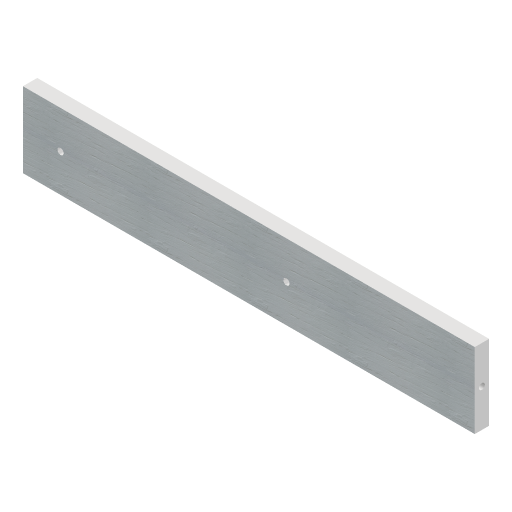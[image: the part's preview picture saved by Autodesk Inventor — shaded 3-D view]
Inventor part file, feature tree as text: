
AUTODESK INVENTOR PART (.ipt)
format: ipt  version: 2024 (Build 280153000, 153)  size: 188,928 bytes
history: native  units: in
note: dims shown in document units (in); Inventor stores cm internally (conversion verified against a paired STEP export)
features: extrude x5, sketch x5
ambient origin geometry x8: Origin, YZ Plane, XZ Plane, XY Plane, X Axis, Y Axis, Z Axis, Center Point
bodies: Solid1 (feature_tree)
feature tree (10):
  extrude  "Extrusion1"  Depth=3.937in
  extrude  "Extrusion2"  Depth=9.8425in
  extrude  "Extrusion3"  Depth=0.315in
  extrude  "Extrusion4"  Depth=0.4331in TaperAngle=0.0deg
  extrude  "Extrusion5"  Depth=0.4331in TaperAngle=0.0deg
  sketch  "Sketch1"  dims[d0=23.622in d1=3.937in]
  sketch  "Sketch2"  dims[d2=0.374in d3=0.374in d4=0.0in d5=0.0in d6=9.8425in]
  sketch  "Sketch3"  dims[d7=1.9685in d8=0.315in]
  sketch  "Sketch4"  dims[d9=0.315in d10=0.4331in d11=0.0in]
  sketch  "Sketch5"  dims[d12=0.315in d13=0.4331in d14=0.0in d15=0.315in d16=0.4331in d17=0.0in d18=1.9685in d19=6.5617in d20=6.5617in d21=6.5617in d22=1.9685in d23=0.315in d24=0.315in d25=0.315in d26=0.315in d27=0.4331in d28=0.0in]
